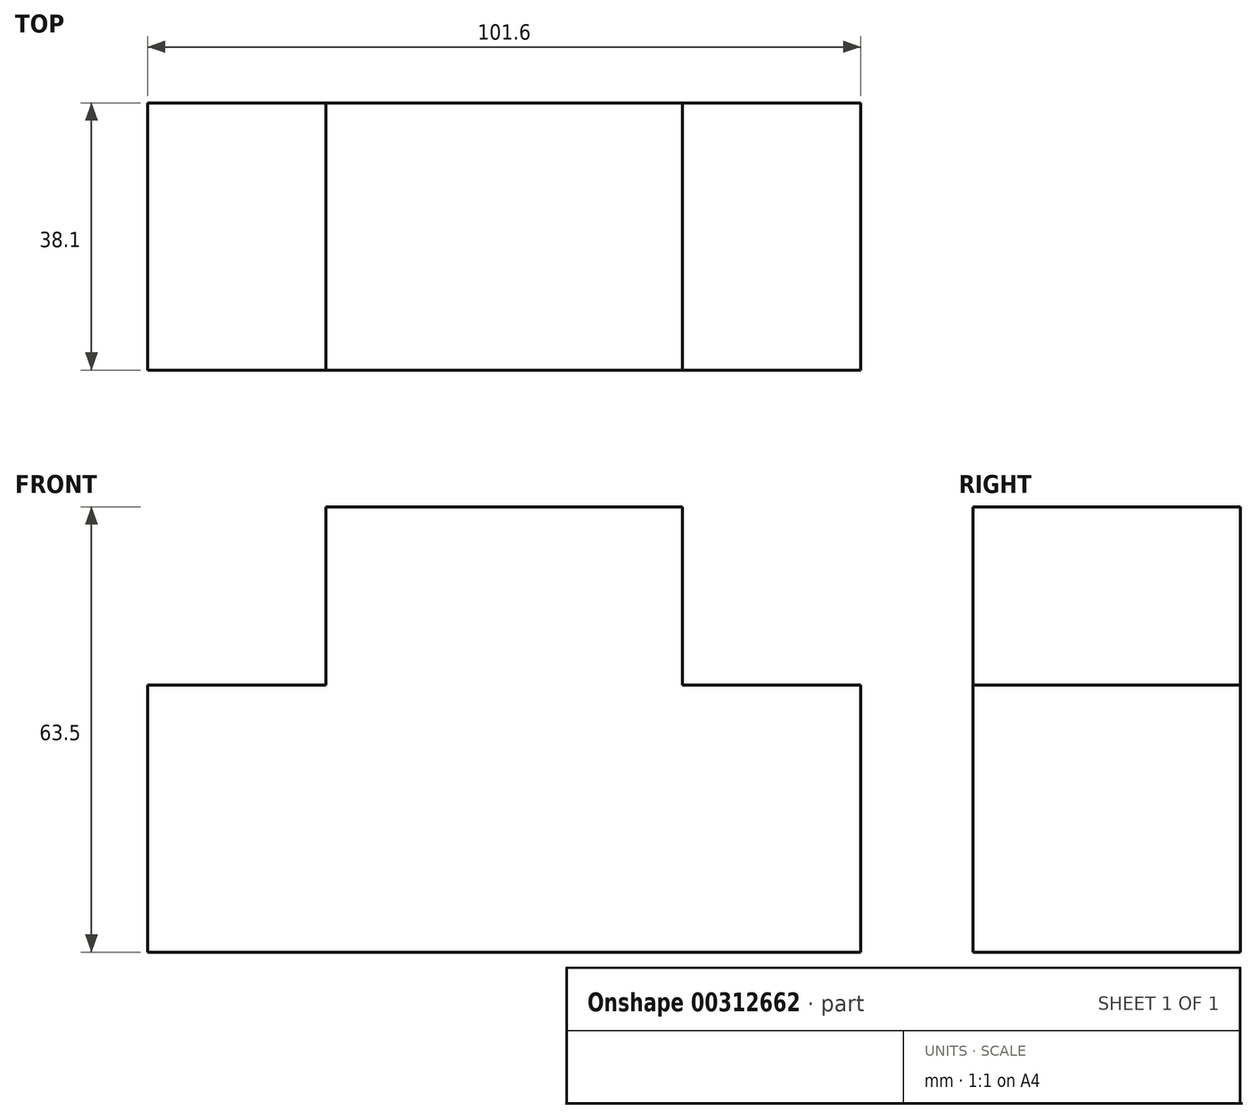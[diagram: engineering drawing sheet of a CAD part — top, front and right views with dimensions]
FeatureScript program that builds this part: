
annotation { "Feature Type Name" : "Feature", "Feature Type Description" : "" }
export const myFeature = defineFeature(function(context is Context, id is Id, definition is map)
    precondition{}
    {
        {
            var Q0;
            Q0=qCreatedBy(makeId("Front.planeOp"),FACE);
            var sketch = newSketch(context, id + "F0", { "sketchPlane" : qUnion([Q0])});
            skLineSegment(sketch, "E0", {"start": v(33.83, -50.9) * mm, "end": v(33.83, -12.8) * mm});
            skLineSegment(sketch, "E1", {"start": v(33.83, -12.8) * mm, "end": v(8.43, -12.8) * mm});
            skLineSegment(sketch, "E2", {"start": v(8.43, -12.8) * mm, "end": v(8.43, 12.6) * mm});
            skLineSegment(sketch, "E3", {"start": v(8.43, 12.6) * mm, "end": v(-42.37, 12.6) * mm});
            skLineSegment(sketch, "E4", {"start": v(-42.37, 12.6) * mm, "end": v(-42.37, -12.8) * mm});
            skLineSegment(sketch, "E5", {"start": v(-42.37, -12.8) * mm, "end": v(-67.77, -12.8) * mm});
            skLineSegment(sketch, "E6", {"start": v(-67.77, -12.8) * mm, "end": v(-67.77, -50.9) * mm});
            skLineSegment(sketch, "E7", {"start": v(-67.77, -50.9) * mm, "end": v(33.83, -50.9) * mm});
            skSolve(sketch);
        }
        {
            var Q0;
            Q0=makeQuery(id+"F0.imprint","IMPRINT",FACE,{"disambiguationData":[TD([[makeQuery(id+"F0.imprint","IMPRINT",EDGE,{"derivedFrom":sQuery(id+"F0.wireOp",EDGE,"E0")}),1.0]])]});
            extrude(context, id + "F1", {"entities" : qUnion([Q0]), "depth" : 38.1 * mm});
        }
    });
